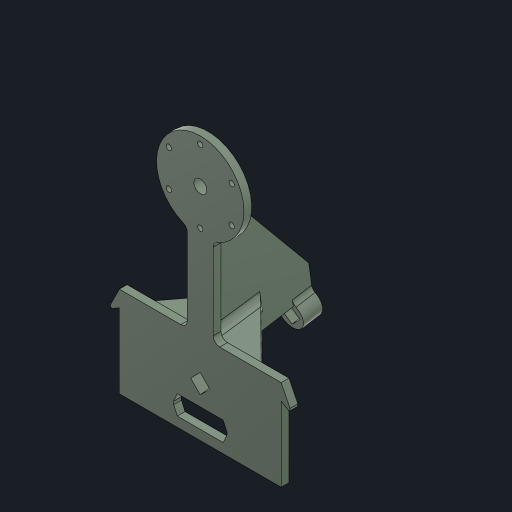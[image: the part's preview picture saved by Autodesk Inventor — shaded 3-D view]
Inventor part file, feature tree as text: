
AUTODESK INVENTOR PART (.ipt)
format: ipt  version: 2023 (Build 270158000, 158)  size: 425,472 bytes
history: native  units: mm
features: extrude x15, sketch x13, other x4, projected_geometry x2, mirror x1, hole x1, pattern_circular x1, fillet x1
ambient origin geometry x8: Origin, YZ Plane, XZ Plane, XY Plane, X Axis, Y Axis, Z Axis, Center Point
bodies: Body1 (feature_tree)
feature tree (38):
  other  "ソリッド1"
  sketch  "スケッチ1"
  extrude  "押し出し1"  Depth=2.4mm
  extrude  "押し出し2"  Depth=40.0mm
  extrude  "押し出し4"  Depth=14.3117mm
  extrude  "爪"  Depth=8.0mm
  extrude  "押し出し17"  Depth=180.0mm
  extrude  "押し出し20"  Depth=15.0mm
  extrude  "押し出し21"  Depth=14.0499mm
  mirror  "ミラー1"
  extrude  "押し出し6"  Depth=30.0mm
  other  "作業平面2"
  extrude  "押し出し10"  Depth=25.0mm TaperAngle=0.0deg
  extrude  "ロッド穴"  Depth=4.0mm TaperAngle=0.0deg
  other  "作業平面3"
  extrude  "押し出し11"  Depth=1.4mm TaperAngle=0.0deg
  hole  "穴1"  [1 undecoded]
  pattern_circular  "円形状パターン1"  [2 undecoded]
  extrude  "穴延長"  Depth=1.4mm TaperAngle=0.0deg
  extrude  "押し出し12"  Depth=1.0mm
  extrude  "押し出し13"  Depth=4.2mm
  fillet  "フィレット2"  [1 undecoded]
  extrude  "押し出し22"  Depth=8.0mm
  sketch  "スケッチ3"
  other  "作業平面1"
  sketch  "スケッチ6"
  sketch  "スケッチ7"
  sketch  "スケッチ8"
  projected_geometry  "投影ループ1"
  sketch  "スケッチ9"
  sketch  "スケッチ10"
  sketch  "スケッチ11"
  sketch  "スケッチ16"
  sketch  "スケッチ19"
  sketch  "スケッチ21"
  sketch  "スケッチ22"
  projected_geometry  "投影ループ2"
  sketch  "スケッチ23"
note: 4 required parameter values undecoded (feature->parameter linkage not recoverable at this tier; creation-order binding heuristic only, values carry confidence <= 0.55)
